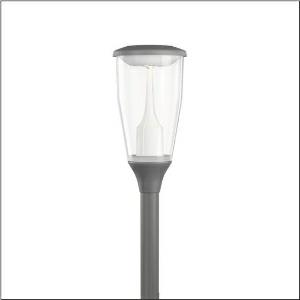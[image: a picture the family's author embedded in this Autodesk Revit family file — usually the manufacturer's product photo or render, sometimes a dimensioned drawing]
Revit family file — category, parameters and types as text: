
# Revit family: dl_11_iq___st1_2a_5xa5565ef14h000022_473d
name_source: partatom
category: Lighting Fixtures
units: mm (PartAtom-declared; Revit-internal decimal feet)

## family parameters
Cut with Voids When Loaded = No
Host = Face
Light Source = No
Part Type = Normal
Room Calculation Point = No
Round Connector Dimension = Use Diameter
Shared = No

## types (1)
- --- (1 x LED, 1560 lm, 10.5 W, 3000K)
    Apparent Load = 11 VA
    CIE Flux Codes = 24 63 94 96 100
    Color Rendering = 70
    Color Temperature = 3000K
    Default Elevation = 1800 mm
    Description = DL 11 iQ, mast luminaire, Module 540 iQ-SR, primary light control with 3 zone facetted reflector, of plastic, silver coated, highly specular, structured, primary optical cover: cover, of PMMA, transparent, light distribution: ST1.2a, light emission: direct distribution, primary light characteristic: asymmetric, installation type: post-top, LED, High Power LED, rated luminous flux: 1.560lm, luminous efficacy: 149lm/W, light colour: 730, colour temperature: 3000K, control gear: iQ Street-Remote, control: Street-Remote, Auto-Match, Temp-Guard, Lumen-Switch, Night-Set, Smart-Wire, Light-Fading, Desk-Remote (wireless, voltage-free reading and setting of iQ features in the workshop via application-optimized NFC function/RFID function), optimised constant luminous flux control (CLO 2.0), mains connection: 220..240V, AC, 50/60Hz, connection cable pre-assembled, cable length: 5,5m, start of lifetime: 11W, end of service life: 11W, reduction: 5W, luminaire housing, upper part, of diecast aluminium, coated, Siteco® metallic grey (DB 702S), spigot size: 60mm (post-top), mounting height: 3..5m, post-top mast mounting element, of diecast aluminium, coated, Siteco® metallic grey (DB 702S), Module 540 iQ-SR, traffic white (RAL 9016), equipment: standard, protection rating (complete): IP66, insulation class (complete): insulation class II (safety insulation), certification: CE, ENEC, ENEC+, VDE, impact resistance: IK07, packaging unit: 1 piece

Light Distribution: ST1.2a
    Height = 665 mm
    Lamp = 1 x LED
    Lamp Light Flux = 1560 lm
    Lamp Power = 10.5 W
    Lamp count = 1
    Length = 334 mm
    Luminous efficacy = 149 lm/W
    Manufacturer = Siteco
    ModVariant = No
    Model = 5XA5565EF14H000022
    Number of Poles = 1
    OnlyDefault = Yes
    Power Factor = 1
    Product Name = DL 11 iQ | ST1.2a
    Product group = mast luminaire | pylon top
    ProductGroupID = 6100
    Protection Class = Protection class II
    Protection Degree = IP 66
    RLX_Detail_Level = 1
    RLX_Emergency_Light_Flux = 0 lm
    RLX_Emergency_Type = 0
    RLX_Emergency_Type_DB = No
    RlxData = <blob elided: 152861 chars, md5=4b1dcf7b>
    Socket = socket
    Standby Power = 0 W
    System Light Flux = 1560 lm
    System Power = 11 W
    Type Comments = factory setting: luminous flux: 100 % | dim-lin: 254 | 419 mA
    Type Image = l_1258354.jpg
    URL = http://relux.com
    VarID = @adj_095170
    Voltage = 0 V
    Weight = 0.00 kg
    Width = 0 mm  [stored 0 ft]

note: [stored X ft] marks values corroborated as IEEE doubles in the binary element streams (Revit-internal decimal feet)

## geometry (parser evidence)
native form markers: Blend x4, Sweep x9
no freeform markers — native parametric forms only
